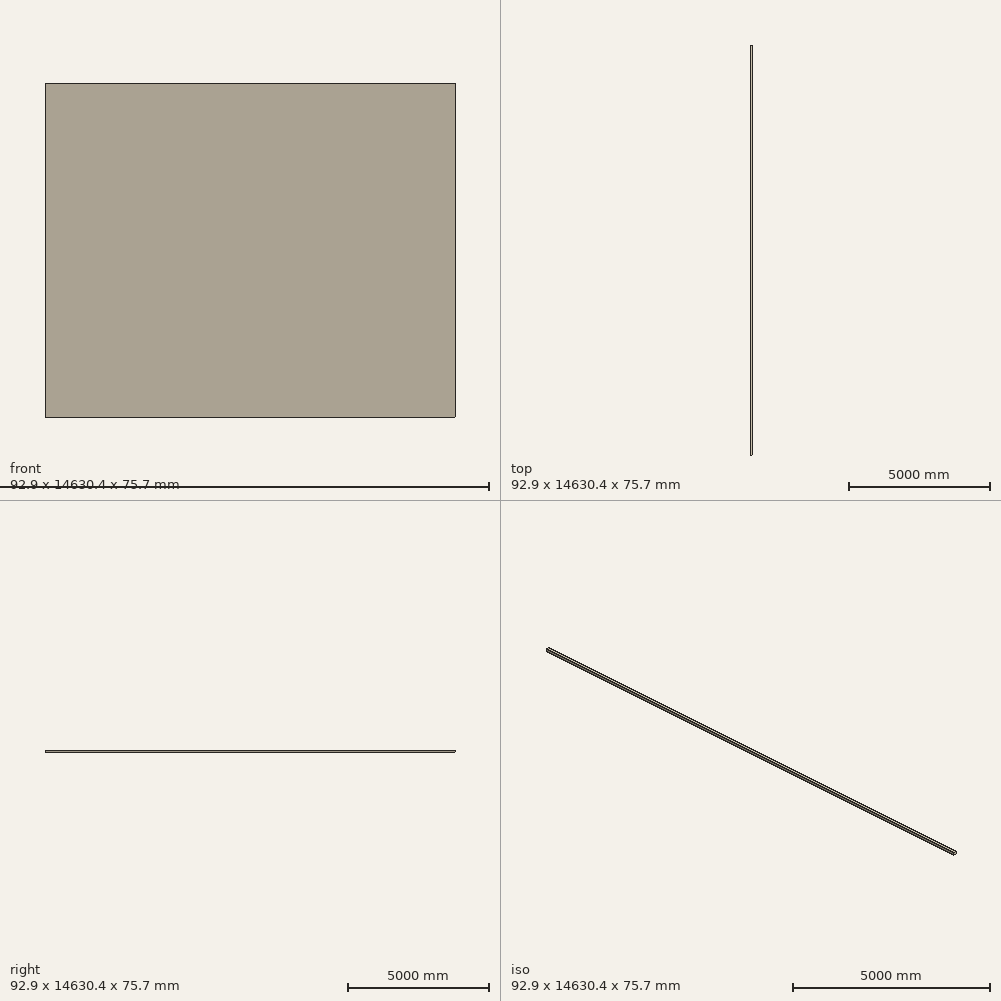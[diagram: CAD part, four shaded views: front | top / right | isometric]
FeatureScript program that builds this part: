
annotation { "Feature Type Name" : "Feature", "Feature Type Description" : "" }
export const myFeature = defineFeature(function(context is Context, id is Id, definition is map)
    precondition{}
    {
        {
            var Q0;
            Q0=qCreatedBy(makeId("Front.planeOp"),FACE);
            var sketch = newSketch(context, id + "F0", { "sketchPlane" : qUnion([Q0])});
            skLineSegment(sketch, "E0.bottom", {"start": v(-35.7, 46.81) * mm, "end": v(57.23, 46.81) * mm});
            skLineSegment(sketch, "E0.top", {"start": v(-35.7, -28.92) * mm, "end": v(57.23, -28.92) * mm});
            skLineSegment(sketch, "E0.left", {"start": v(-35.7, 46.81) * mm, "end": v(-35.7, -28.92) * mm});
            skLineSegment(sketch, "E0.right", {"start": v(57.23, 46.81) * mm, "end": v(57.23, -28.92) * mm});
            skSolve(sketch);
        }
        {
            var Q0;
            Q0 = qSketchRegion(id + "F0", true);
            extrude(context, id + "F1", {"entities" : qUnion([Q0]), "depth" : 14630.4 * mm});
        }
    });
